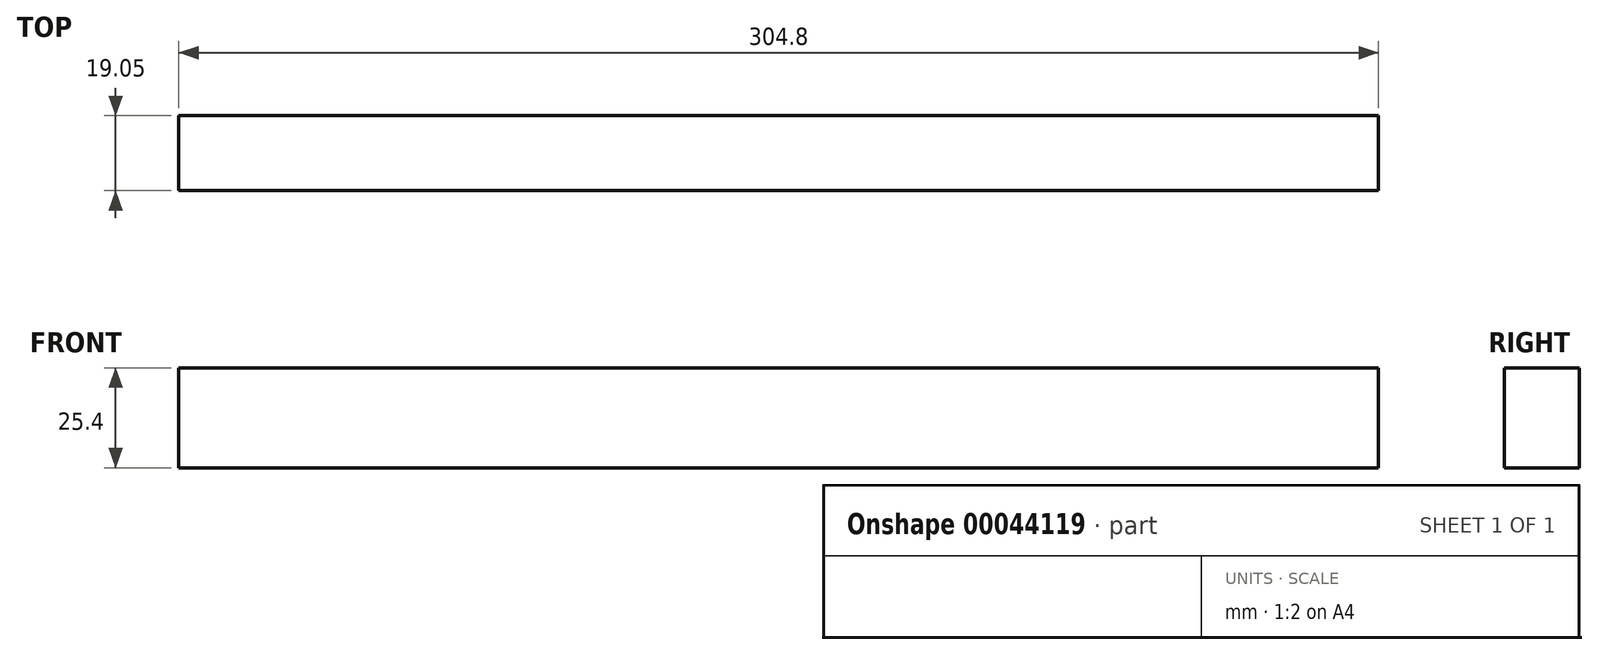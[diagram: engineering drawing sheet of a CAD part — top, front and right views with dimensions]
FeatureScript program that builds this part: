
annotation { "Feature Type Name" : "Feature", "Feature Type Description" : "" }
export const myFeature = defineFeature(function(context is Context, id is Id, definition is map)
    precondition{}
    {
        {
            var Q0;
            Q0=qCreatedBy(makeId("Front.planeOp"),FACE);
            var sketch = newSketch(context, id + "F0", { "sketchPlane" : qUnion([Q0])});
            skLineSegment(sketch, "E0.rect.bottom", {"start": v(152.4, 12.7) * mm, "end": v(-152.4, 12.7) * mm});
            skLineSegment(sketch, "E0.rect.top", {"start": v(152.4, -12.7) * mm, "end": v(-152.4, -12.7) * mm});
            skLineSegment(sketch, "E0.rect.left", {"start": v(152.4, 12.7) * mm, "end": v(152.4, -12.7) * mm});
            skLineSegment(sketch, "E0.rect.right", {"start": v(-152.4, 12.7) * mm, "end": v(-152.4, -12.7) * mm});
            skPoint(sketch, "E0.rect.middle", {"position": v(0, 0) * mm});
            skSolve(sketch);
        }
        {
            var Q0;
            Q0=makeQuery(id+"F0.imprint","IMPRINT",FACE,{"disambiguationData":[TD([[makeQuery(id+"F0.imprint","IMPRINT",EDGE,{"derivedFrom":sQuery(id+"F0.wireOp",EDGE,"E0.rect.bottom")}),1.0]])]});
            extrude(context, id + "F1", {"entities" : qUnion([Q0]), "depth" : 19.05 * mm});
        }
    });
